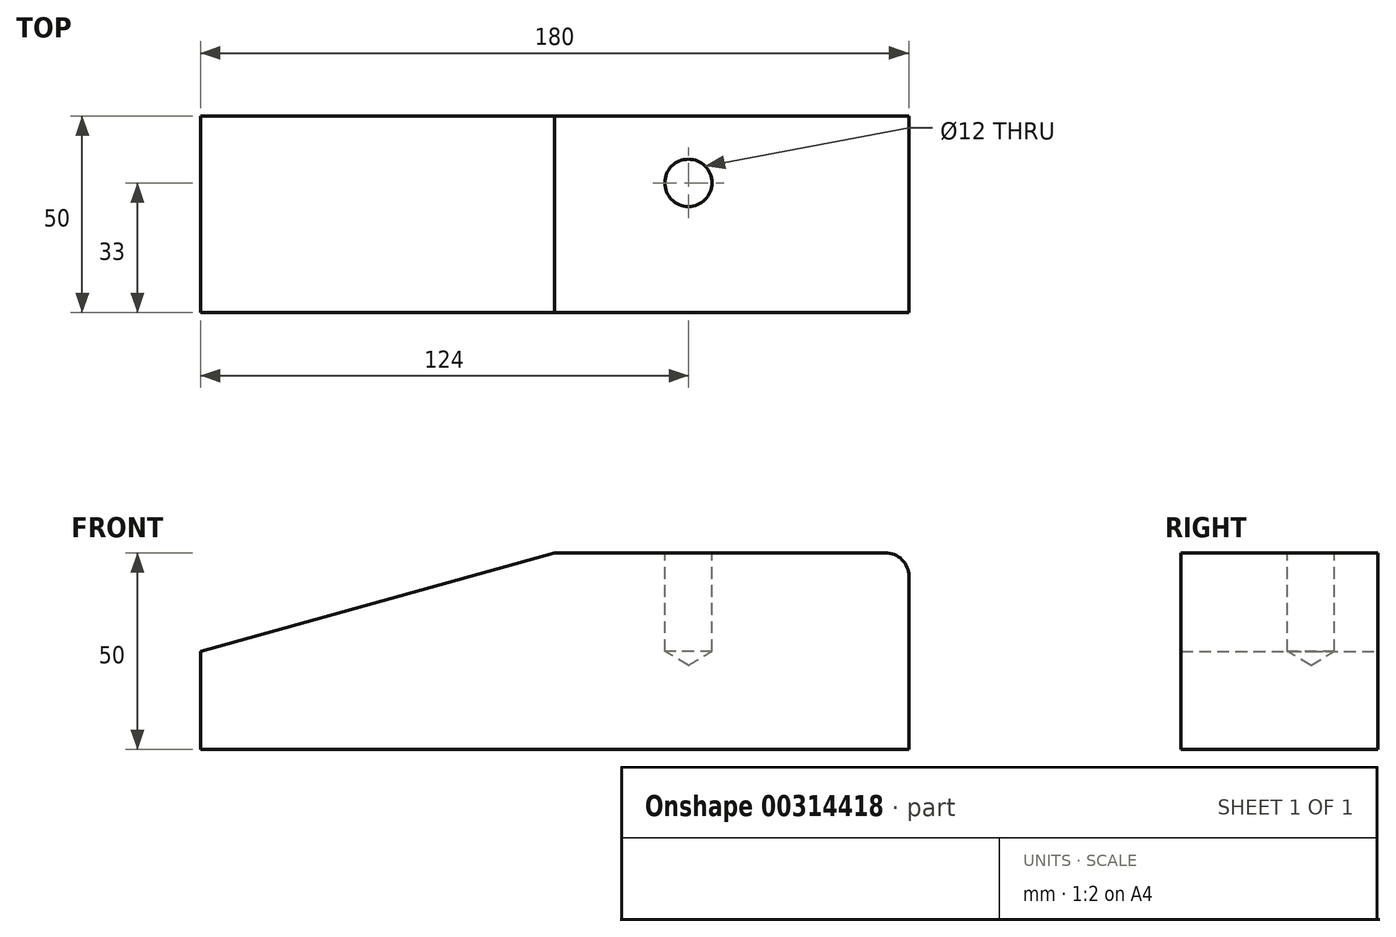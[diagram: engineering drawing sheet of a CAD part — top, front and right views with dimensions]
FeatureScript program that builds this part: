
annotation { "Feature Type Name" : "Feature", "Feature Type Description" : "" }
export const myFeature = defineFeature(function(context is Context, id is Id, definition is map)
    precondition{}
    {
        {
            var Q0;
            Q0=qCreatedBy(makeId("Front.planeOp"),FACE);
            var sketch = newSketch(context, id + "F0", { "sketchPlane" : qUnion([Q0])});
            skLineSegment(sketch, "E0.top", {"start": v(-90, -25) * mm, "end": v(90, -25) * mm});
            skLineSegment(sketch, "E0.right", {"start": v(90, 19) * mm, "end": v(90, -25) * mm});
            skPoint(sketch, "E0.middle", {"position": v(0, 0) * mm});
            skLineSegment(sketch, "E1", {"start": v(0, 25) * mm, "end": v(84, 25) * mm});
            skLineSegment(sketch, "E2", {"start": v(-90, 0) * mm, "end": v(-90, -25) * mm});
            skPoint(sketch, "E3.visualSharp", {"position": v(90, 25) * mm});
            skArc(sketch, "E3.filletArc", {"start": v(90, 19) * mm, "mid": v(88.24, 23.24) * mm, "end": v(84, 25) * mm});
            skLineSegment(sketch, "E4", {"start": v(-90, 0) * mm, "end": v(0, 25) * mm});
            skSolve(sketch);
        }
        {
            var Q0;
            Q0 = qSketchRegion(id + "F0", true);
            extrude(context, id + "F1", {"entities" : qUnion([Q0]), "depth" : 50 * mm});
        }
        {
            var Q0;
            Q0=makeQuery(id+"F1.opExtrude","SWEPT_FACE",FACE,{"disambiguationData":[OSD([sQuery(id+"F0.wireOp",EDGE,"E1")])]});
            var sketch = newSketch(context, id + "F2", { "sketchPlane" : qUnion([Q0])});
            skCircle(sketch, "E5", {"center": v(34, -17) * mm, "radius": 6 * mm});
            skSolve(sketch);
        }
        {
            var Q0;
            Q0=sQuery(id+"F2.wireOp",VERTEX,"E5.center");
            var Q1;
            Q1=makeQuery(id+"F1.opExtrude","SWEPT_BODY",BODY,{"disambiguationData":[OSD([sQuery(id+"F0.wireOp",EDGE,"E0.top"),sQuery(id+"F0.wireOp",EDGE,"E0.right"),sQuery(id+"F0.wireOp",EDGE,"CiJGvlZj-wB0k-MYaW-hIE5-anmOExSoHd4V"),sQuery(id+"F0.wireOp",EDGE,"E1"),sQuery(id+"F0.wireOp",EDGE,"E2"),sQuery(id+"F0.wireOp",EDGE,"E3.filletArc")])]});
            hole(context, id + "F3", {"style" : HoleStyle.SIMPLE, "endStyle" : HoleEndStyle.BLIND, "holeDiameter" : 12 * mm, "holeDepth" : 25 * mm, "tappedDepth" : 12.7 * mm, "tapClearance" : 3, "locations" : qUnion([Q0]), "scope" : qUnion([Q1])});
        }
    });
